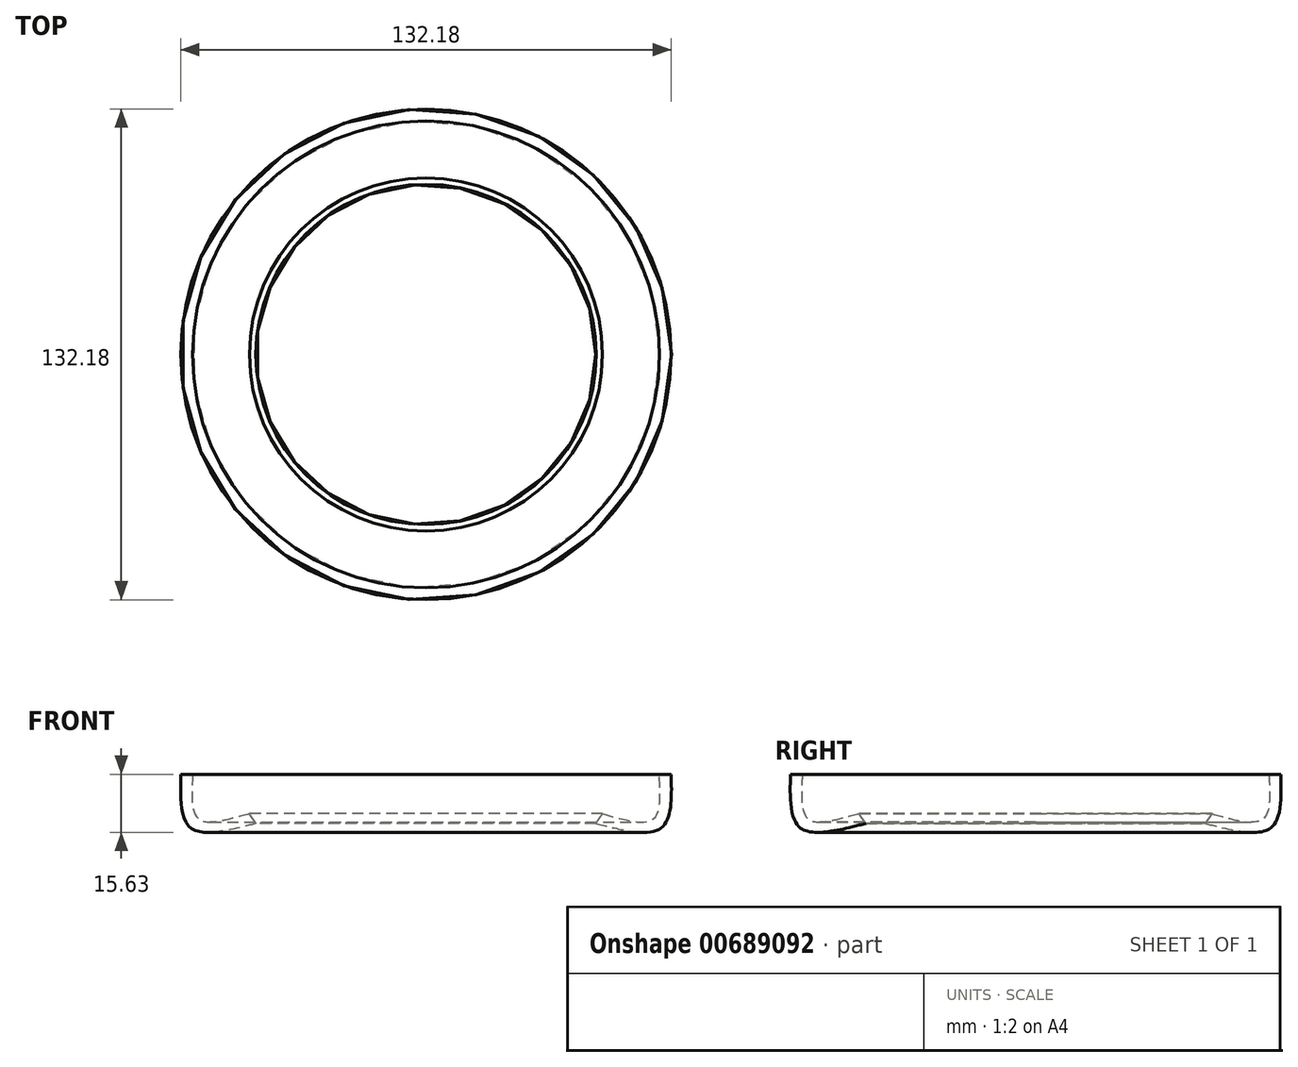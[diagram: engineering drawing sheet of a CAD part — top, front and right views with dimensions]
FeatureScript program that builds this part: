
annotation { "Feature Type Name" : "Feature", "Feature Type Description" : "" }
export const myFeature = defineFeature(function(context is Context, id is Id, definition is map)
    precondition{}
    {
        {
            var Q0;
            Q0=qCreatedBy(makeId("Front.planeOp"),FACE);
            var sketch = newSketch(context, id + "F0", { "sketchPlane" : qUnion([Q0])});
            skLineSegment(sketch, "E0", {"start": v(0, 0) * mm, "end": v(0, -10.93) * mm});
            skFitSpline(sketch, "E1", {"points": [v(-45.73, -13.24) * mm, v(-46.64, -0.52) * mm], "startDerivative": vector(-10.17, 16.47) * mm, "endDerivative": vector(0.5, 16.23) * mm});
            skFitSpline(sketch, "E2", {"points": [v(-45.73, -13.24) * mm, v(-63.07, -14.6) * mm, v(-66.04, 0) * mm], "startDerivative": vector(-31.39, -7.08) * mm, "endDerivative": vector(0.48, 35.54) * mm});
            skFitSpline(sketch, "E3", {"points": [v(-47.52, -10.63) * mm, v(-61.1, -12.11) * mm, v(-62.87, 0) * mm], "startDerivative": vector(-26.1, -6.69) * mm, "endDerivative": vector(0.47, 29.15) * mm});
            skLineSegment(sketch, "E4", {"start": v(-66.04, 0) * mm, "end": v(-62.87, 0) * mm});
            skLineSegment(sketch, "E5", {"start": v(-47.52, -10.63) * mm, "end": v(-45.82, -13.1) * mm});
            skSolve(sketch);
        }
        {
            var Q0;
            Q0=makeQuery(id+"F0.imprint","IMPRINT",FACE,{"disambiguationData":[TD([[makeQuery(id+"F0.imprint","IMPRINT",EDGE,{"derivedFrom":sQuery(id+"F0.wireOp",EDGE,"E1")}),1.0]])]});
            var Q1;
            Q1=sQuery(id+"F0.wireOp",EDGE,"E0");
            revolve(context, id + "F1", {"entities" : qUnion([Q0]), "axis" : qUnion([Q1]), "revolveType" : RevolveType.FULL});
        }
    });
